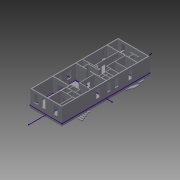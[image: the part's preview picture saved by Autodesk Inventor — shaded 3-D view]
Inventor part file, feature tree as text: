
AUTODESK INVENTOR PART (.ipt)
format: ipt  version: 2013 SP2 (Build 170200200, 200)  size: 644,608 bytes
history: native  units: in
note: dims shown in document units (in); Inventor stores cm internally (conversion verified against a paired STEP export)
features: extrude x11, sketch x11, projected_geometry x2, other x1, imported_body x1
ambient origin geometry x8: Origin, YZ Plane, XZ Plane, XY Plane, X Axis, Y Axis, Z Axis, Center Point
bodies: Solid1 (feature_tree)
feature tree (26):
  other  "2nd Floor1"
  extrude  "Extrusion1"  Depth=1.0in TaperAngle=0.0deg
  extrude  "Extrusion2"  Depth=36.0in TaperAngle=0.0deg
  extrude  "Extrusion3"  Depth=7.25in
  extrude  "Extrusion5"  Depth=36.0in TaperAngle=0.0deg
  sketch  "Sketch6"  dims[d45=7.25in d46=7.25in]
  extrude  "Extrusion7"  Depth=7.25in
  extrude  "Extrusion8"  Depth=105.0in
  extrude  "Extrusion9"  Depth=9.5in
  extrude  "Extrusion10"  Depth=7.0in
  extrude  "Extrusion11"  Depth=7.0in
  extrude  "Extrusion12"  Depth=7.0in
  extrude  "Extrusion13"  Depth=7.0in
  sketch  "3D Sketch1"
  imported_body  "Base1"
  sketch  "Sketch1"  dims[d0=1.0in d1=0.0in d2=1.0in d3=0.0in]
  sketch  "Sketch2"  dims[d4=7.25in d5=7.25in d6=7.25in d7=10.5in d8=10.5in d9=10.5in d12=36.0in d13=0.0in]
  sketch  "Sketch3"  dims[d14=10.5in d15=10.5in d16=10.5in d17=10.5in d18=10.5in d19=10.5in d20=7.25in d21=7.25in d22=7.25in d23=7.25in d24=7.25in d25=7.25in d26=10.5in d27=7.25in d28=10.5in d29=10.5in d30=10.5in d31=10.5in d32=10.5in d33=7.25in d34=7.25in d35=7.25in d36=7.25in d37=7.25in d39=7.25in]
  sketch  "Sketch4"  dims[d40=10.5in d43=36.0in d44=0.0in]
  sketch  "Sketch7"  dims[d47=16.0in d70=105.0in]
  projected_geometry  "Projected Loop1"
  sketch  "Sketch8"  dims[d72=66.5in d73=9.5in]
  sketch  "Sketch9"  dims[d74=3.5in d75=7.0in]
  projected_geometry  "Projected Loop2"
  sketch  "Sketch10"  dims[d76=7.0in d77=7.0in]
  sketch  "Sketch11"  dims[d78=7.0in d79=7.0in d80=7.0in d81=7.0in d82=9.5in d83=9.5in d84=9.5in d85=9.5in d86=9.5in d87=9.5in d88=38.0in d89=0.0in d90=41.0in d91=0.0in d93=10.0in d94=10.0in d95=10.0in d96=12.0in d97=12.0in d99=11.0in d100=10.0in d101=10.0in d102=12.0in d103=12.0in d104=10.0in d105=12.0in d106=105.5in d107=10.0in d108=12.0in d109=10.0in d110=12.0in d111=10.0in d112=10.0in d113=12.0in d114=12.0in d115=30.0in d116=0.0in d117=30.0in d118=0.0in d119=30.0in d120=0.0in d121=1.0in d122=0.0in d123=26.25in d125=179.5276in d126=1.0in d127=0.0in]
